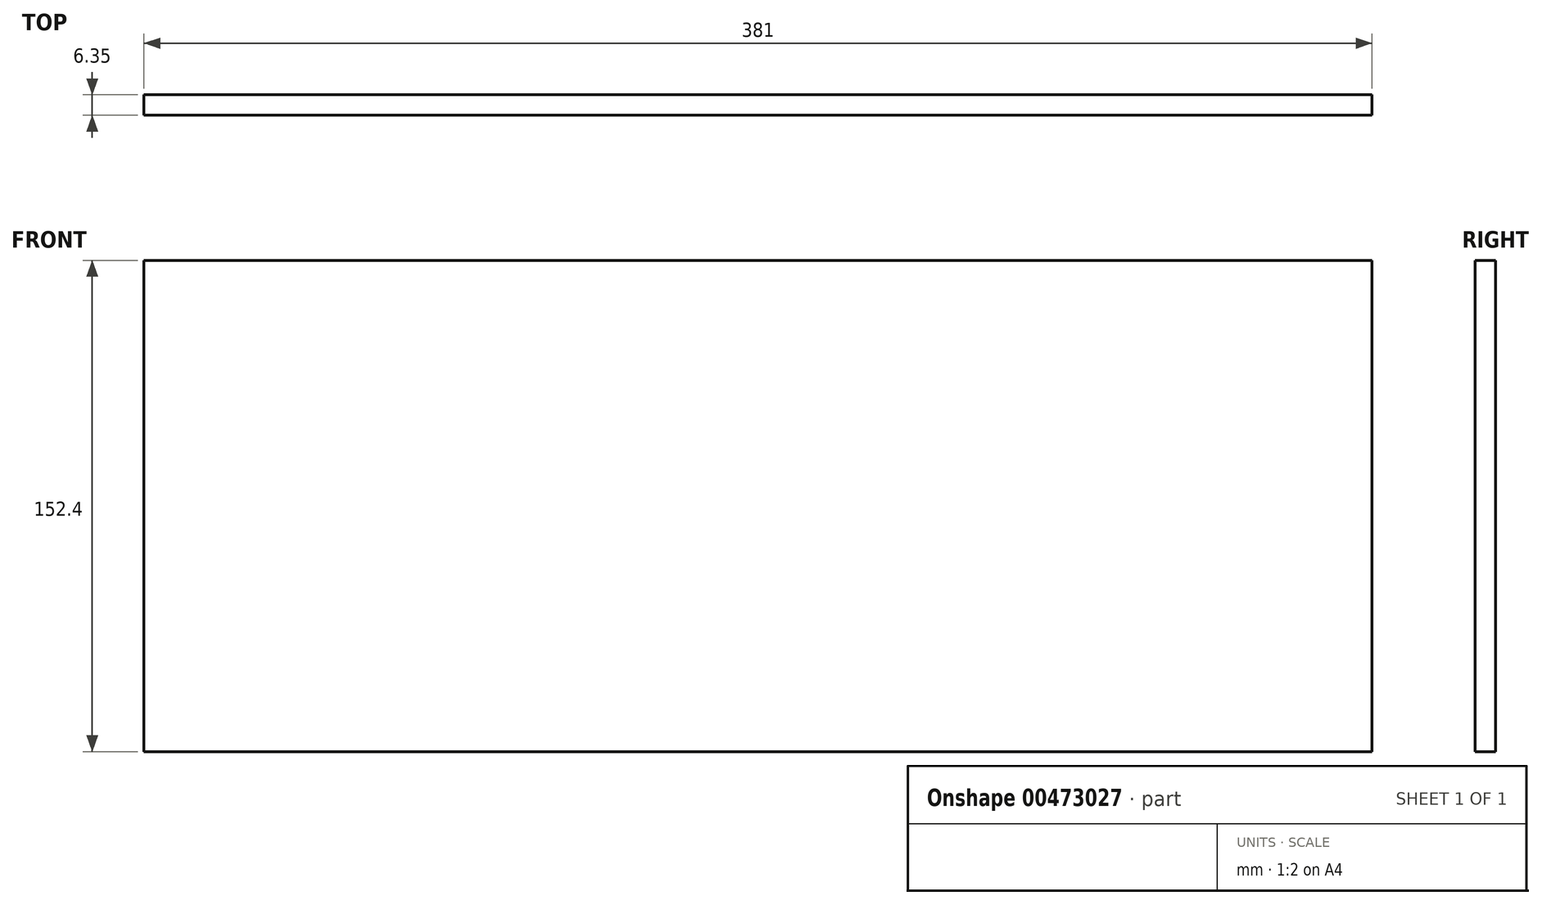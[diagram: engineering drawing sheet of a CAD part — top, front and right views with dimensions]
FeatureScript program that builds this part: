
annotation { "Feature Type Name" : "Feature", "Feature Type Description" : "" }
export const myFeature = defineFeature(function(context is Context, id is Id, definition is map)
    precondition{}
    {
        {
            var Q0;
            Q0=qCreatedBy(makeId("Front.planeOp"),FACE);
            var sketch = newSketch(context, id + "F0", { "sketchPlane" : qUnion([Q0])});
            skLineSegment(sketch, "E0.bottom", {"start": v(190.5, 76.2) * mm, "end": v(-190.5, 76.2) * mm});
            skLineSegment(sketch, "E0.top", {"start": v(190.5, -76.2) * mm, "end": v(-190.5, -76.2) * mm});
            skLineSegment(sketch, "E0.left", {"start": v(190.5, 76.2) * mm, "end": v(190.5, -76.2) * mm});
            skLineSegment(sketch, "E0.right", {"start": v(-190.5, 76.2) * mm, "end": v(-190.5, -76.2) * mm});
            skPoint(sketch, "E0.middle", {"position": v(0, 0) * mm});
            skSolve(sketch);
        }
        {
            var Q0;
            Q0=makeQuery(id+"F0.imprint","IMPRINT",FACE,{"disambiguationData":[TD([[makeQuery(id+"F0.imprint","IMPRINT",EDGE,{"derivedFrom":sQuery(id+"F0.wireOp",EDGE,"E0.bottom")}),1.0]])]});
            extrude(context, id + "F1", {"entities" : qUnion([Q0]), "depth" : 6.35 * mm});
        }
    });
